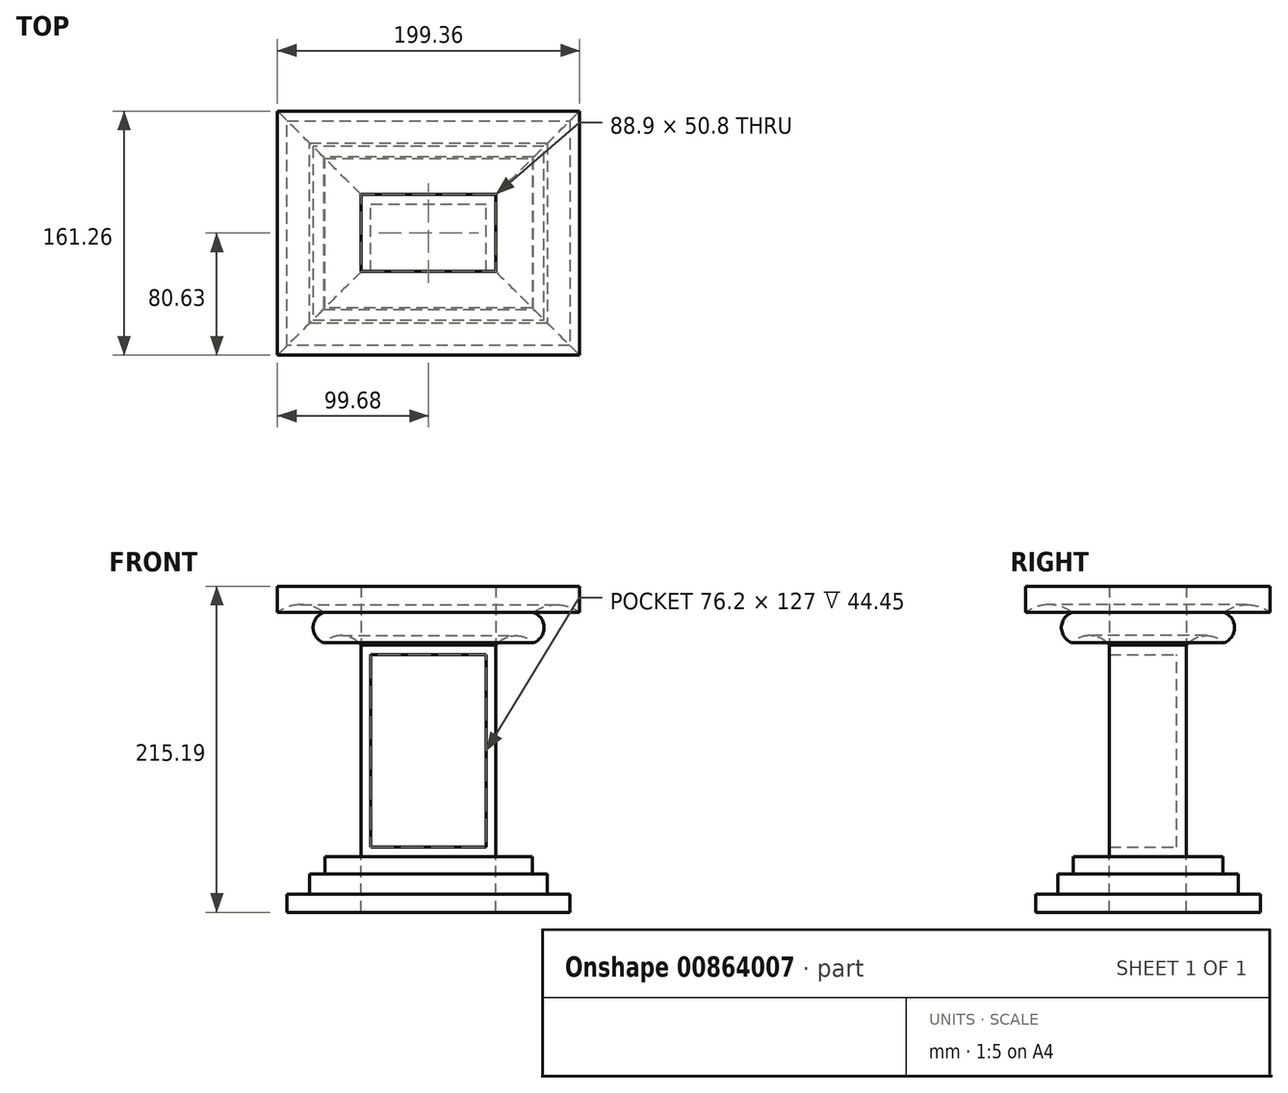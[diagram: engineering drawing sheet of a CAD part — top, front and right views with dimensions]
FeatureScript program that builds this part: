
annotation { "Feature Type Name" : "Feature", "Feature Type Description" : "" }
export const myFeature = defineFeature(function(context is Context, id is Id, definition is map)
    precondition{}
    {
        {
            var Q0;
            Q0=qCreatedBy(makeId("Front.planeOp"),FACE);
            var sketch = newSketch(context, id + "F0", { "sketchPlane" : qUnion([Q0])});
            skLineSegment(sketch, "E0.bottom", {"start": v(0, 0) * mm, "end": v(88.9, 0) * mm});
            skLineSegment(sketch, "E0.top", {"start": v(0, 139.7) * mm, "end": v(88.9, 139.7) * mm});
            skLineSegment(sketch, "E0.left", {"start": v(0, 0) * mm, "end": v(0, 139.7) * mm});
            skLineSegment(sketch, "E0.right", {"start": v(88.9, 0) * mm, "end": v(88.9, 139.7) * mm});
            skSolve(sketch);
        }
        {
            var Q0;
            Q0=makeQuery(id+"F0.imprint","IMPRINT",FACE,{"disambiguationData":[TD([[makeQuery(id+"F0.imprint","IMPRINT",EDGE,{"derivedFrom":sQuery(id+"F0.wireOp",EDGE,"E0.bottom")}),1.0]])]});
            extrude(context, id + "F1", {"entities" : qUnion([Q0]), "depth" : 50.8 * mm, "offsetDistance" : 25.4 * mm});
        }
        {
            var Q0;
            Q0=makeQuery(id+"F1.opExtrude","CAP_FACE",FACE,{"disambiguationData":[OSD([sQuery(id+"F0.wireOp",EDGE,"E0.bottom"),sQuery(id+"F0.wireOp",EDGE,"E0.top"),sQuery(id+"F0.wireOp",EDGE,"E0.left"),sQuery(id+"F0.wireOp",EDGE,"E0.right")])],"isStart":false});
            shell(context, id + "F2", {"entities" : qUnion([Q0]), "thickness" : 6.35 * mm});
        }
        {
            var Q0;
            Q0=makeQuery(id+"F1.opExtrude","SWEPT_FACE",FACE,{"disambiguationData":[OSD([sQuery(id+"F0.wireOp",EDGE,"E0.top")])]});
            var sketch = newSketch(context, id + "F3", { "sketchPlane" : qUnion([Q0])});
            skLineSegment(sketch, "E1", {"start": v(0, 0) * mm, "end": v(0, -50.8) * mm});
            skLineSegment(sketch, "E2", {"start": v(0, -50.8) * mm, "end": v(88.9, -50.8) * mm});
            skLineSegment(sketch, "E3", {"start": v(88.9, -50.8) * mm, "end": v(88.9, 0) * mm});
            skSolve(sketch);
        }
        {
            var Q0;
            Q0=makeQuery(id+"F1.opExtrude","CAP_FACE",FACE,{"disambiguationData":[OSD([sQuery(id+"F0.wireOp",EDGE,"E0.bottom"),sQuery(id+"F0.wireOp",EDGE,"E0.top"),sQuery(id+"F0.wireOp",EDGE,"E0.left"),sQuery(id+"F0.wireOp",EDGE,"E0.right")])],"isStart":true});
            var sketch = newSketch(context, id + "F4", { "sketchPlane" : qUnion([Q0])});
            skLineSegment(sketch, "E4", {"start": v(0, 139.7) * mm, "end": v(0, 178.64) * mm});
            skLineSegment(sketch, "E5", {"start": v(0, 178.64) * mm, "end": v(55.23, 178.64) * mm});
            skLineSegment(sketch, "E6", {"start": v(55.23, 178.64) * mm, "end": v(55.23, 161.33) * mm});
            skArc(sketch, "E7", {"start": v(55.23, 161.33) * mm, "mid": v(40.02, 166.48) * mm, "end": v(24.81, 161.33) * mm});
            skArc(sketch, "E8", {"start": v(24.81, 141.4) * mm, "mid": v(31.76, 151.37) * mm, "end": v(24.81, 161.33) * mm});
            skArc(sketch, "E9", {"start": v(24.81, 141.4) * mm, "mid": v(12.03, 146.02) * mm, "end": v(0, 139.7) * mm});
            skSolve(sketch);
        }
        {
            var Q0;
            Q0=makeQuery(id+"F4.imprint","IMPRINT",FACE,{"disambiguationData":[TD([[makeQuery(id+"F4.imprint","IMPRINT",EDGE,{"derivedFrom":sQuery(id+"F4.wireOp",EDGE,"E4")}),-1.0]])]});
            var Q1;
            Q1=makeQuery(id+"F1.opExtrude","CAP_EDGE",EDGE,{"disambiguationData":[OSD([sQuery(id+"F0.wireOp",EDGE,"E0.top")])],"isStart":true});
            var Q2;
            Q2=sQuery(id+"F3.wireOp",EDGE,"E1");
            var Q3;
            Q3=sQuery(id+"F3.wireOp",EDGE,"E2");
            var Q4;
            Q4=sQuery(id+"F3.wireOp",EDGE,"E3");
            sweep(context, id + "F5", {"profiles" : qUnion([Q0]), "path" : qUnion([Q1, Q2, Q3, Q4])});
        }
        {
            var Q0;
            Q0=makeQuery(id+"F1.opExtrude","SWEPT_FACE",FACE,{"disambiguationData":[OSD([sQuery(id+"F0.wireOp",EDGE,"E0.bottom")])]});
            var sketch = newSketch(context, id + "F6", { "sketchPlane" : qUnion([Q0])});
            skLineSegment(sketch, "E10", {"start": v(88.9, 50.8) * mm, "end": v(88.9, 0) * mm});
            skLineSegment(sketch, "E11", {"start": v(88.9, 0) * mm, "end": v(0, 0) * mm});
            skLineSegment(sketch, "E12", {"start": v(0, 0) * mm, "end": v(0, 50.8) * mm});
            skSolve(sketch);
        }
        {
            var Q0;
            Q0=makeQuery(id+"F1.opExtrude","CAP_FACE",FACE,{"disambiguationData":[OSD([sQuery(id+"F0.wireOp",EDGE,"E0.bottom"),sQuery(id+"F0.wireOp",EDGE,"E0.top"),sQuery(id+"F0.wireOp",EDGE,"E0.left"),sQuery(id+"F0.wireOp",EDGE,"E0.right")])],"isStart":true});
            var sketch = newSketch(context, id + "F7", { "sketchPlane" : qUnion([Q0])});
            skLineSegment(sketch, "E13", {"start": v(-88.9, 0) * mm, "end": v(-88.9, -36.55) * mm});
            skLineSegment(sketch, "E14", {"start": v(-88.9, -36.55) * mm, "end": v(-137.74, -36.55) * mm});
            skLineSegment(sketch, "E15", {"start": v(-137.74, -36.55) * mm, "end": v(-137.74, -24.48) * mm});
            skLineSegment(sketch, "E16", {"start": v(-137.74, -24.48) * mm, "end": v(-122.9, -24.48) * mm});
            skLineSegment(sketch, "E17", {"start": v(-122.9, -24.48) * mm, "end": v(-122.9, -11.38) * mm});
            skLineSegment(sketch, "E18", {"start": v(-122.9, -11.38) * mm, "end": v(-112.9, -11.38) * mm});
            skLineSegment(sketch, "E19", {"start": v(-112.9, -11.38) * mm, "end": v(-112.9, 0) * mm});
            skLineSegment(sketch, "E20", {"start": v(-112.9, 0) * mm, "end": v(-88.9, 0) * mm});
            skSolve(sketch);
        }
        {
            var Q0;
            Q0=makeQuery(id+"F7.imprint","IMPRINT",FACE,{"disambiguationData":[TD([[makeQuery(id+"F7.imprint","IMPRINT",EDGE,{"derivedFrom":sQuery(id+"F7.wireOp",EDGE,"E13")}),-1.0]])]});
            var Q1;
            Q1=sQuery(id+"F6.wireOp",EDGE,"E10");
            var Q2;
            Q2=makeQuery(id+"F1.opExtrude","CAP_EDGE",EDGE,{"disambiguationData":[OSD([sQuery(id+"F0.wireOp",EDGE,"E0.bottom")])],"isStart":false});
            var Q3;
            Q3=sQuery(id+"F6.wireOp",EDGE,"E12");
            var Q4;
            Q4=sQuery(id+"F6.wireOp",EDGE,"E11");
            sweep(context, id + "F8", {"profiles" : qUnion([Q0]), "path" : qUnion([Q1, Q2, Q3, Q4])});
        }
    });
